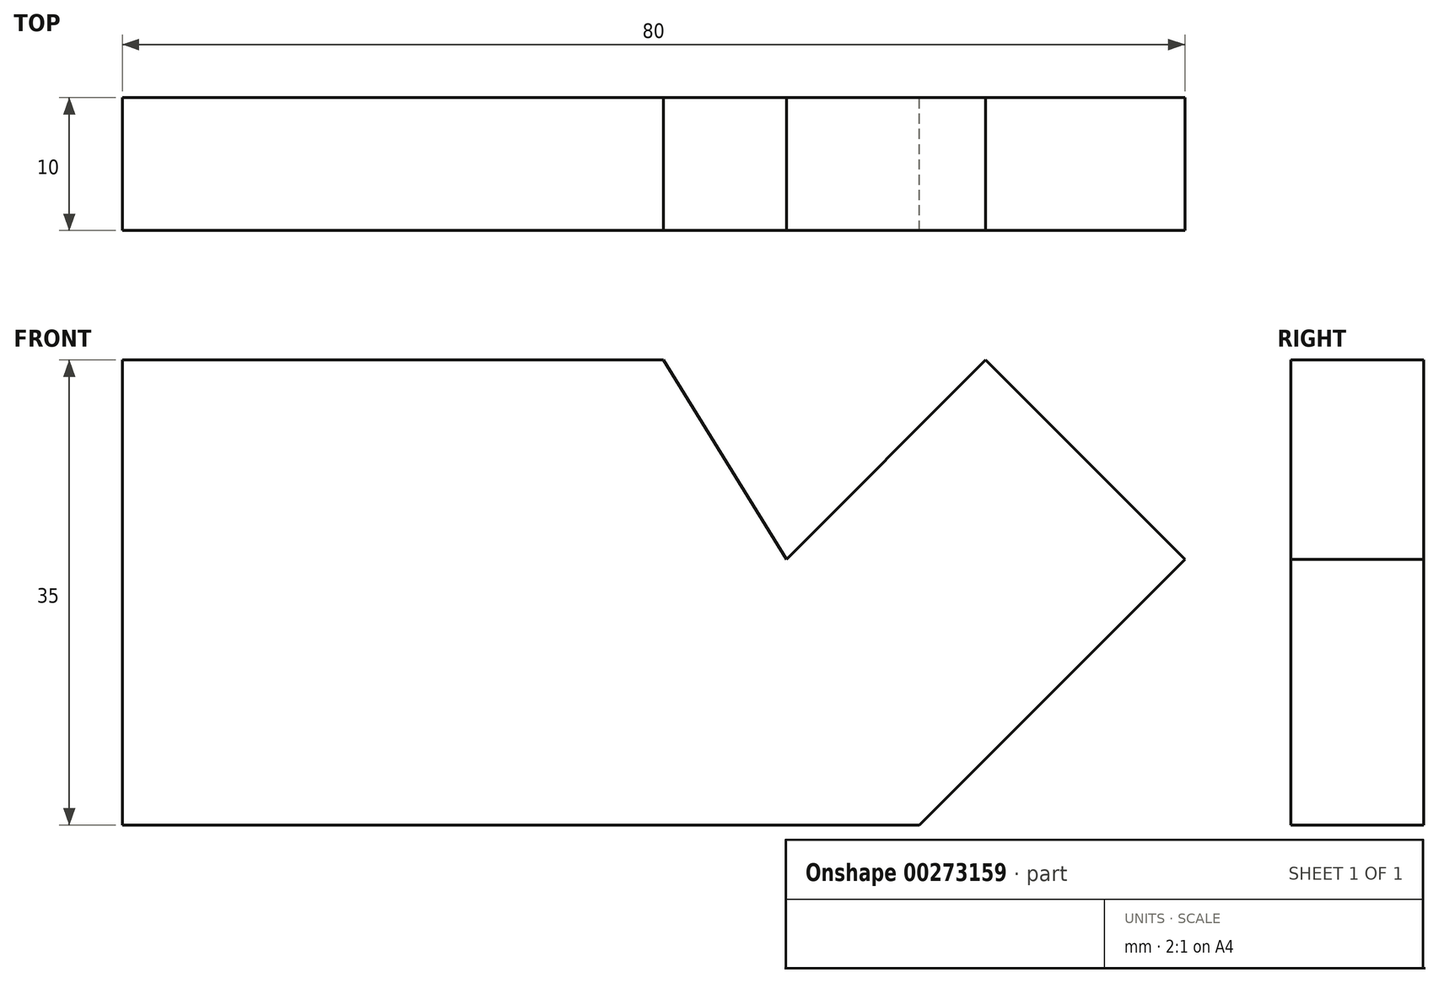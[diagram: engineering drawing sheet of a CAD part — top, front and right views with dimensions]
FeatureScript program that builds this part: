
annotation { "Feature Type Name" : "Feature", "Feature Type Description" : "" }
export const myFeature = defineFeature(function(context is Context, id is Id, definition is map)
    precondition{}
    {
        {
            var Q0;
            Q0=qCreatedBy(makeId("Front.planeOp"),FACE);
            var sketch = newSketch(context, id + "F0", { "sketchPlane" : qUnion([Q0])});
            skLineSegment(sketch, "E0", {"start": v(0, 0) * mm, "end": v(60, 0) * mm});
            skLineSegment(sketch, "E1", {"start": v(0, 0) * mm, "end": v(0, 35) * mm});
            skLineSegment(sketch, "E2", {"start": v(0, 35) * mm, "end": v(40.73, 35) * mm});
            skLineSegment(sketch, "E3", {"start": v(60, 0) * mm, "end": v(80, 20) * mm});
            skLineSegment(sketch, "E4", {"start": v(80, 20) * mm, "end": v(65, 35) * mm});
            skLineSegment(sketch, "E5", {"start": v(65, 35) * mm, "end": v(50, 20) * mm});
            skLineSegment(sketch, "E6", {"start": v(50, 20) * mm, "end": v(40.73, 35) * mm});
            skSolve(sketch);
        }
        {
            var Q0;
            Q0 = qSketchRegion(id + "F0", true);
            extrude(context, id + "F1", {"entities" : qUnion([Q0]), "depth" : 10 * mm});
        }
    });
